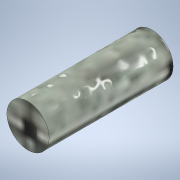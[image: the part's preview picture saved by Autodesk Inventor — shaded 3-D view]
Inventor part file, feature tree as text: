
AUTODESK INVENTOR PART (.ipt)
format: ipt  version: 2020 (Build 240168000, 168)  size: 123,904 bytes
history: native  units: mm
features: extrude x1, sketch x1
ambient origin geometry x8: Origin, YZ Plane, XZ Plane, XY Plane, X Axis, Y Axis, Z Axis, Center Point
bodies: Solid1 (feature_tree)
feature tree (2):
  extrude  "Extrusion1"  Depth=220.0mm TaperAngle=0.0deg
  sketch  "Sketch1"  dims[d0=75.0mm d1=220.0mm d2=0.0mm]
